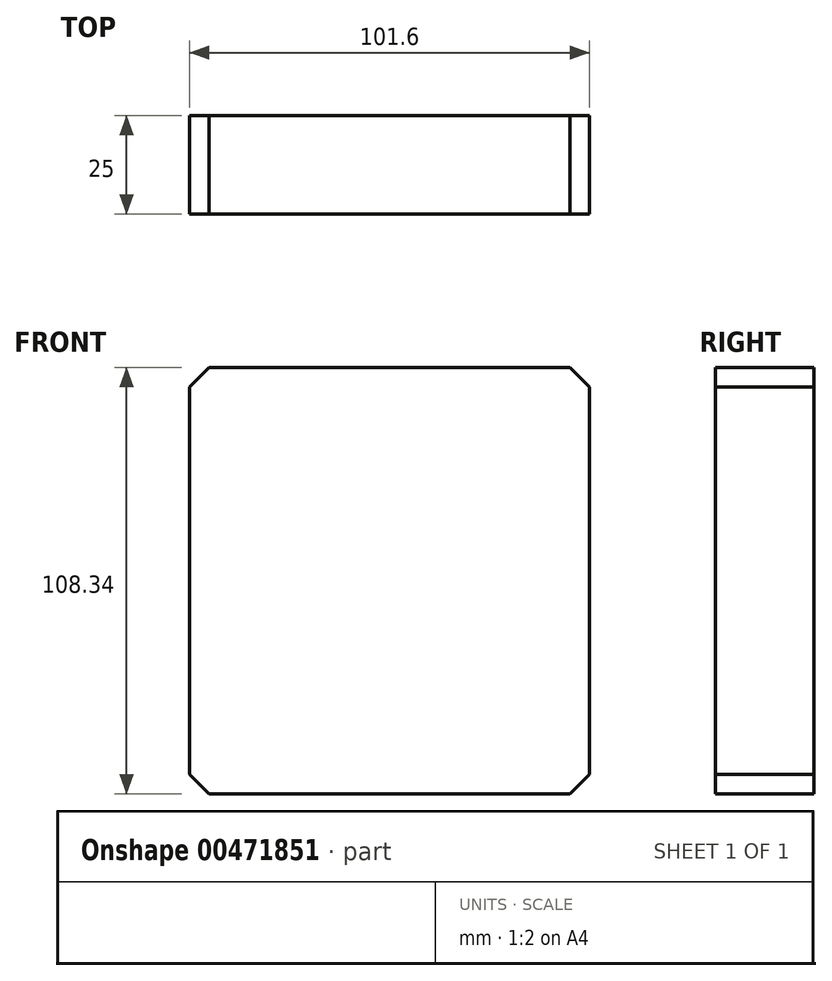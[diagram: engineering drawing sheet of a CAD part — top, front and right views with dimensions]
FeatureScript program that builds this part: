
annotation { "Feature Type Name" : "Feature", "Feature Type Description" : "" }
export const myFeature = defineFeature(function(context is Context, id is Id, definition is map)
    precondition{}
    {
        {
            var Q0;
            Q0=qCreatedBy(makeId("Front.planeOp"),FACE);
            var sketch = newSketch(context, id + "F0", { "sketchPlane" : qUnion([Q0])});
            skLineSegment(sketch, "E0.bottom", {"start": v(50.8, -54.17) * mm, "end": v(-50.8, -54.17) * mm});
            skLineSegment(sketch, "E0.top", {"start": v(50.8, 54.17) * mm, "end": v(-50.8, 54.17) * mm});
            skLineSegment(sketch, "E0.left", {"start": v(50.8, -54.17) * mm, "end": v(50.8, 54.17) * mm});
            skLineSegment(sketch, "E0.right", {"start": v(-50.8, -54.17) * mm, "end": v(-50.8, 54.17) * mm});
            skPoint(sketch, "E0.middle", {"position": v(0, 0) * mm});
            skSolve(sketch);
        }
        {
            var Q0;
            Q0=makeQuery(id+"F0.imprint","IMPRINT",FACE,{"disambiguationData":[TD([[makeQuery(id+"F0.imprint","IMPRINT",EDGE,{"derivedFrom":sQuery(id+"F0.wireOp",EDGE,"E0.bottom")}),-1.0]])]});
            extrude(context, id + "F1", {"entities" : qUnion([Q0]), "depth" : 25 * mm});
        }
        {
            var Q0;
            Q0=makeQuery(id+"F1.opExtrude","SWEPT_EDGE",EDGE,{"disambiguationData":[OSD([sQuery(id+"F0.wireOp",EDGE,"E0.top"),sQuery(id+"F0.wireOp",EDGE,"E0.left")])]});
            var Q1;
            Q1=makeQuery(id+"F1.opExtrude","SWEPT_EDGE",EDGE,{"disambiguationData":[OSD([sQuery(id+"F0.wireOp",EDGE,"E0.top"),sQuery(id+"F0.wireOp",EDGE,"E0.right")])]});
            var Q2;
            Q2=makeQuery(id+"F1.opExtrude","SWEPT_EDGE",EDGE,{"disambiguationData":[OSD([sQuery(id+"F0.wireOp",EDGE,"E0.bottom"),sQuery(id+"F0.wireOp",EDGE,"E0.right")])]});
            var Q3;
            Q3=makeQuery(id+"F1.opExtrude","SWEPT_EDGE",EDGE,{"disambiguationData":[OSD([sQuery(id+"F0.wireOp",EDGE,"E0.bottom"),sQuery(id+"F0.wireOp",EDGE,"E0.left")])]});
            chamfer(context, id + "F2", {"entities" : qUnion([Q0, Q1, Q2, Q3]), "width" : 5 * mm, "tangentPropagation" : true});
        }
    });
